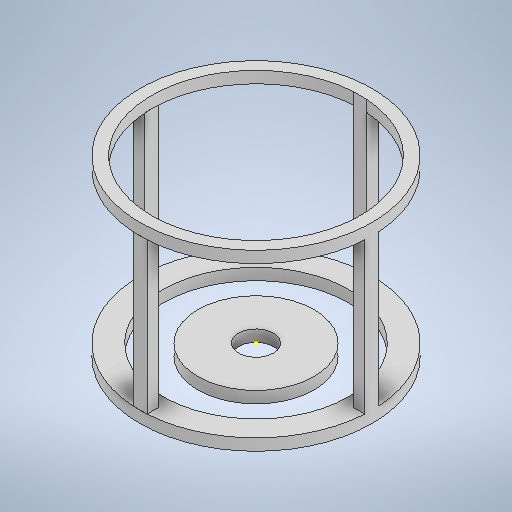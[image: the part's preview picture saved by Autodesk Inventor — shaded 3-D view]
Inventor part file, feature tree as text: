
AUTODESK INVENTOR PART (.ipt)
format: ipt  version: 2025 (Build 290162000, 162)  size: 330,752 bytes
history: native  units: mm
features: sketch x10, extrude x9, other x1
ambient origin geometry x8: Origin, YZ Plane, XZ Plane, XY Plane, X Axis, Y Axis, Z Axis, Center Point
bodies: Body1 (feature_tree)
feature tree (20):
  other  "Bryła1"
  extrude  "Wyciągnięcie proste1"  Depth=100.0mm
  extrude  "Wyciągnięcie proste2"  Depth=80.0mm TaperAngle=0.0deg
  sketch  "Szkic3"
  extrude  "Wyciągnięcie proste3"  Depth=90.0mm
  extrude  "Wyciągnięcie proste4"  Depth=75.0mm TaperAngle=0.0deg
  extrude  "Wyciągnięcie proste5"  Depth=15.0mm
  extrude  "Wyciągnięcie proste6"  Depth=75.0mm TaperAngle=0.0deg
  extrude  "Wyciągnięcie proste7"  Depth=75.0mm TaperAngle=0.0deg
  extrude  "Wyciągnięcie proste8"  Depth=10.0mm TaperAngle=0.0deg
  extrude  "Wyciągnięcie proste9"  Depth=5.0mm TaperAngle=0.0deg
  sketch  "Szkic1"
  sketch  "Szkic2"
  sketch  "Szkic4"
  sketch  "Szkic9"
  sketch  "Szkic10"
  sketch  "Szkic11"
  sketch  "Szkic12"
  sketch  "Szkic13"
  sketch  "Szkic14"
